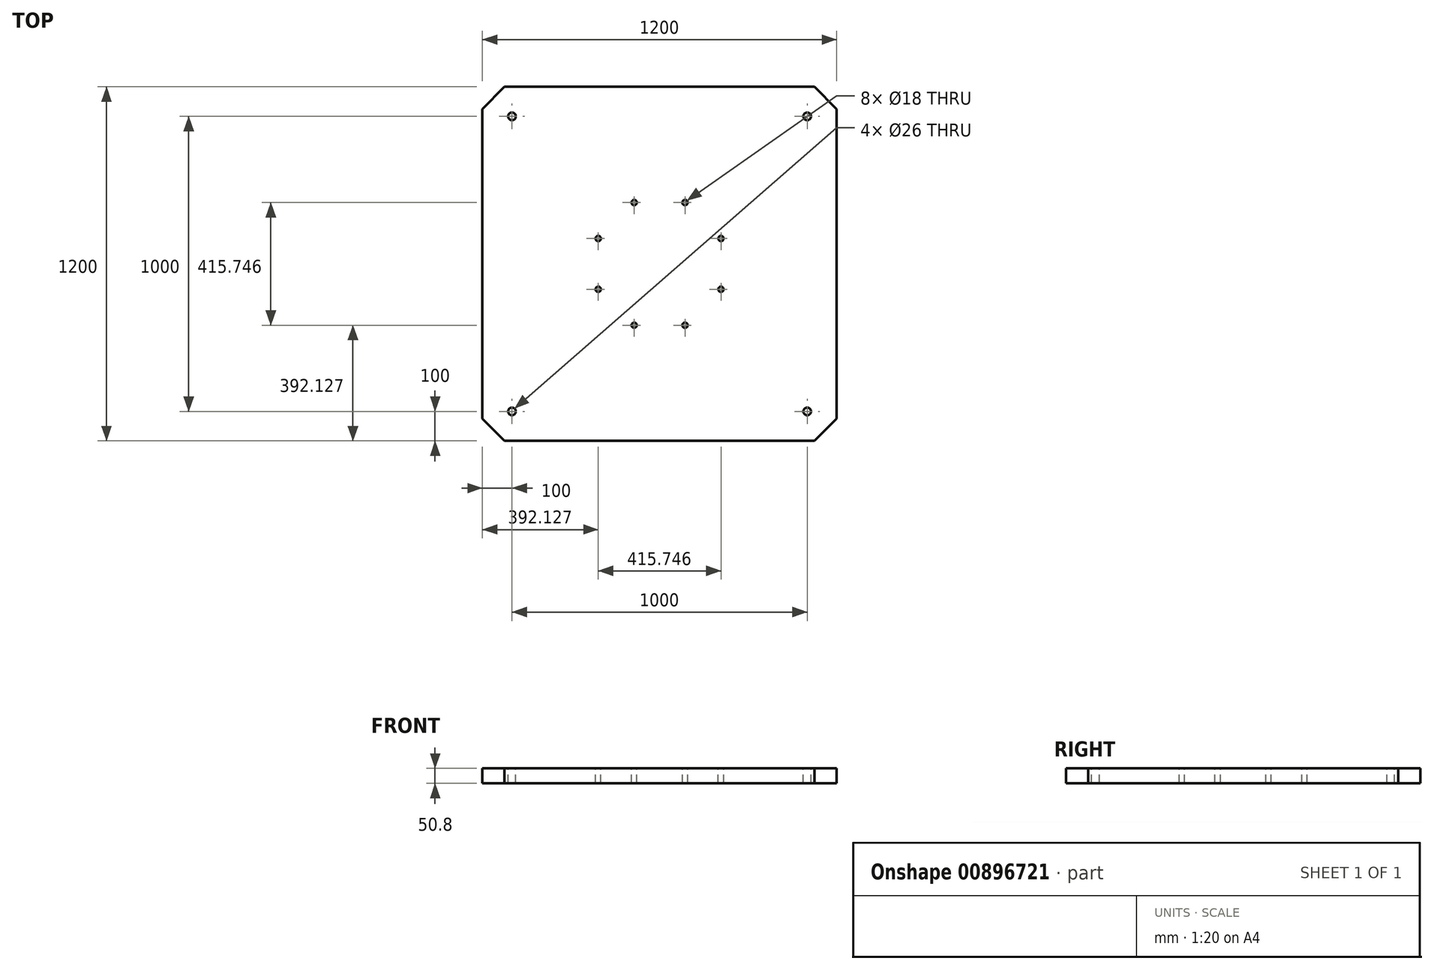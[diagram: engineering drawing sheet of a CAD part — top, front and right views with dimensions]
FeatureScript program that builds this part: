
annotation { "Feature Type Name" : "Feature", "Feature Type Description" : "" }
export const myFeature = defineFeature(function(context is Context, id is Id, definition is map)
    precondition{}
    {
        {
            var Q0;
            Q0=qCreatedBy(makeId("Top.planeOp"),FACE);
            var sketch = newSketch(context, id + "F0", { "sketchPlane" : qUnion([Q0])});
            skLineSegment(sketch, "E0.bottom", {"start": v(600, 600) * mm, "end": v(-600, 600) * mm});
            skLineSegment(sketch, "E0.top", {"start": v(600, -600) * mm, "end": v(-600, -600) * mm});
            skLineSegment(sketch, "E0.left", {"start": v(600, 600) * mm, "end": v(600, -600) * mm});
            skLineSegment(sketch, "E0.right", {"start": v(-600, 600) * mm, "end": v(-600, -600) * mm});
            skPoint(sketch, "E0.middle", {"position": v(0, 0) * mm});
            skSolve(sketch);
        }
        {
            var Q0;
            Q0 = qSketchRegion(id + "F0", true);
            extrude(context, id + "F1", {"entities" : qUnion([Q0]), "endBound" : BoundingType.SYMMETRIC, "depth" : 50.8 * mm, "offsetDistance" : 25.4 * mm});
        }
        {
            var Q0;
            Q0=makeQuery(id+"F1.opExtrude","CAP_FACE",FACE,{"disambiguationData":[OSD([sQuery(id+"F0.wireOp",EDGE,"E0.bottom"),sQuery(id+"F0.wireOp",EDGE,"E0.top"),sQuery(id+"F0.wireOp",EDGE,"E0.left"),sQuery(id+"F0.wireOp",EDGE,"E0.right")])],"isStart":false});
            var sketch = newSketch(context, id + "F2", { "sketchPlane" : qUnion([Q0])});
            skCircle(sketch, "E1", {"center": v(0, 0) * mm, "radius": 225 * mm, "construction": true});
            skLineSegment(sketch, "E2", {"start": v(0, 0) * mm, "end": v(-86.1, 207.87) * mm, "construction": true});
            skLineSegment(sketch, "E3", {"start": v(0, 0) * mm, "end": v(0, 225) * mm, "construction": true});
            skLineSegment(sketch, "E4", {"start": v(0, 0) * mm, "end": v(86.1, 207.87) * mm, "construction": true});
            skLineSegment(sketch, "E5", {"start": v(0, 0) * mm, "end": v(207.87, 86.1) * mm, "construction": true});
            skLineSegment(sketch, "E6", {"start": v(0, 0) * mm, "end": v(-207.87, 86.1) * mm, "construction": true});
            skLineSegment(sketch, "E7", {"start": v(0, 0) * mm, "end": v(-207.87, -86.1) * mm, "construction": true});
            skLineSegment(sketch, "E8", {"start": v(0, 0) * mm, "end": v(-86.1, -207.87) * mm, "construction": true});
            skLineSegment(sketch, "E9", {"start": v(0, 0) * mm, "end": v(86.1, -207.87) * mm, "construction": true});
            skLineSegment(sketch, "E10", {"start": v(0, 0) * mm, "end": v(207.87, -86.1) * mm, "construction": true});
            skSolve(sketch);
        }
        {
            var Q0;
            Q0=sQuery(id+"F2.wireOp",VERTEX,"E2.end");
            var Q1;
            Q1=sQuery(id+"F2.wireOp",VERTEX,"E4.end");
            var Q2;
            Q2=sQuery(id+"F2.wireOp",VERTEX,"E5.end");
            var Q3;
            Q3=sQuery(id+"F2.wireOp",VERTEX,"E10.end");
            var Q4;
            Q4=sQuery(id+"F2.wireOp",VERTEX,"E9.end");
            var Q5;
            Q5=sQuery(id+"F2.wireOp",VERTEX,"E8.end");
            var Q6;
            Q6=sQuery(id+"F2.wireOp",VERTEX,"E7.end");
            var Q7;
            Q7=sQuery(id+"F2.wireOp",VERTEX,"E6.end");
            var Q8;
            Q8=makeQuery(id+"F1.opExtrude","SWEPT_BODY",BODY,{"disambiguationData":[OSD([sQuery(id+"F0.wireOp",EDGE,"E0.bottom"),sQuery(id+"F0.wireOp",EDGE,"E0.top"),sQuery(id+"F0.wireOp",EDGE,"E0.left"),sQuery(id+"F0.wireOp",EDGE,"E0.right")])]});
            hole(context, id + "F3", {"style" : HoleStyle.SIMPLE, "endStyle" : HoleEndStyle.THROUGH, "standardTappedOrClearance" : lookupTablePath({ "standard" : "ISO", "engagement" : "75%", "pitch" : "2 mm", "size" : "M20", "type" : "Tapped" }), "standardBlindInLast" : lookupTablePath({ "standard" : "ISO", "engagement" : "75%", "pitch" : "2 mm", "size" : "M20", "type" : "Tapped" }), "holeDiameter" : 18 * mm, "majorDiameter" : 20 * mm, "showTappedDepth" : true, "isTappedThrough" : true, "tappedDepth" : 12.7 * mm, "tapClearance" : 3, "startFromSketch" : true, "locations" : qUnion([Q0, Q1, Q2, Q3, Q4, Q5, Q6, Q7]), "scope" : qUnion([Q8])});
        }
        {
            var Q0;
            Q0=makeQuery(id+"F1.opExtrude","SWEPT_EDGE",EDGE,{"disambiguationData":[OSD([sQuery(id+"F0.wireOp",EDGE,"E0.bottom"),sQuery(id+"F0.wireOp",EDGE,"E0.right")])]});
            var Q1;
            Q1=makeQuery(id+"F1.opExtrude","SWEPT_EDGE",EDGE,{"disambiguationData":[OSD([sQuery(id+"F0.wireOp",EDGE,"E0.bottom"),sQuery(id+"F0.wireOp",EDGE,"E0.left")])]});
            var Q2;
            Q2=makeQuery(id+"F1.opExtrude","SWEPT_EDGE",EDGE,{"disambiguationData":[OSD([sQuery(id+"F0.wireOp",EDGE,"E0.top"),sQuery(id+"F0.wireOp",EDGE,"E0.left")])]});
            var Q3;
            Q3=makeQuery(id+"F1.opExtrude","SWEPT_EDGE",EDGE,{"disambiguationData":[OSD([sQuery(id+"F0.wireOp",EDGE,"E0.top"),sQuery(id+"F0.wireOp",EDGE,"E0.right")])]});
            chamfer(context, id + "F4", {"entities" : qUnion([Q0, Q1, Q2, Q3]), "width" : 75 * mm, "tangentPropagation" : true});
        }
        {
            var Q0;
            Q0=makeQuery(id+"F1.opExtrude","CAP_FACE",FACE,{"disambiguationData":[OSD([sQuery(id+"F0.wireOp",EDGE,"E0.bottom"),sQuery(id+"F0.wireOp",EDGE,"E0.top"),sQuery(id+"F0.wireOp",EDGE,"E0.left"),sQuery(id+"F0.wireOp",EDGE,"E0.right")])],"isStart":false});
            var sketch = newSketch(context, id + "F5", { "sketchPlane" : qUnion([Q0])});
            skLineSegment(sketch, "E11.bottom", {"start": v(500, -500) * mm, "end": v(-500, -500) * mm, "construction": true});
            skLineSegment(sketch, "E11.top", {"start": v(500, 500) * mm, "end": v(-500, 500) * mm, "construction": true});
            skLineSegment(sketch, "E11.left", {"start": v(500, -500) * mm, "end": v(500, 500) * mm, "construction": true});
            skLineSegment(sketch, "E11.right", {"start": v(-500, -500) * mm, "end": v(-500, 500) * mm, "construction": true});
            skPoint(sketch, "E11.middle", {"position": v(0, 0) * mm});
            skSolve(sketch);
        }
        {
            var Q0;
            Q0=sQuery(id+"F5.wireOp",VERTEX,"E11.top.start");
            var Q1;
            Q1=sQuery(id+"F5.wireOp",VERTEX,"E11.bottom.start");
            var Q2;
            Q2=sQuery(id+"F5.wireOp",VERTEX,"E11.top.end");
            var Q3;
            Q3=sQuery(id+"F5.wireOp",VERTEX,"E11.bottom.end");
            var Q4;
            Q4=makeQuery(id+"F1.opExtrude","SWEPT_BODY",BODY,{"disambiguationData":[OSD([sQuery(id+"F0.wireOp",EDGE,"E0.bottom"),sQuery(id+"F0.wireOp",EDGE,"E0.top"),sQuery(id+"F0.wireOp",EDGE,"E0.left"),sQuery(id+"F0.wireOp",EDGE,"E0.right")])]});
            hole(context, id + "F6", {"style" : HoleStyle.SIMPLE, "endStyle" : HoleEndStyle.THROUGH, "holeDiameter" : 26 * mm, "majorDiameter" : 20 * mm, "isTappedThrough" : true, "tappedDepth" : 12.7 * mm, "tapClearance" : 3, "startFromSketch" : true, "locations" : qUnion([Q0, Q1, Q2, Q3]), "scope" : qUnion([Q4])});
        }
    });
